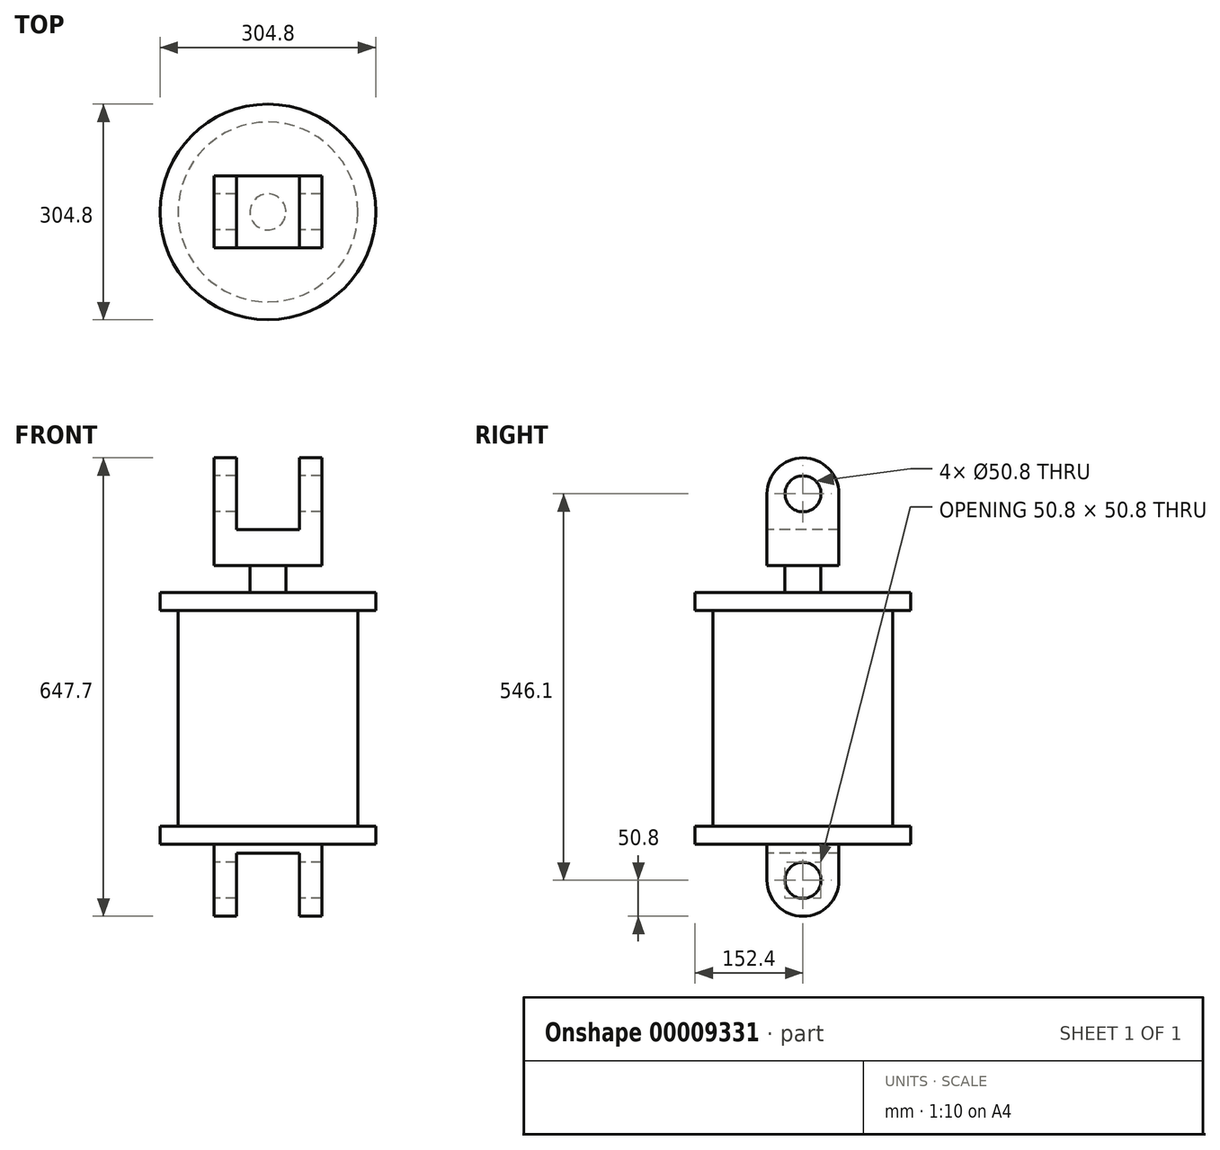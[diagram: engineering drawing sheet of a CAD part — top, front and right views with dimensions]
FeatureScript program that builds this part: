
annotation { "Feature Type Name" : "Feature", "Feature Type Description" : "" }
export const myFeature = defineFeature(function(context is Context, id is Id, definition is map)
    precondition{}
    {
        {
            var Q0;
            Q0=qCreatedBy(makeId("Right.planeOp"),FACE);
            var sketch = newSketch(context, id + "F0", { "sketchPlane" : qUnion([Q0])});
            skCircle(sketch, "E0", {"center": v(0, 0) * mm, "radius": 25.4 * mm});
            skArc(sketch, "E1", {"start": v(-50.8, 0) * mm, "mid": v(0, -50.8) * mm, "end": v(50.8, 0) * mm});
            skLineSegment(sketch, "E2", {"start": v(-50.8, 0) * mm, "end": v(-50.8, 50.8) * mm});
            skLineSegment(sketch, "E3", {"start": v(-50.8, 50.8) * mm, "end": v(50.8, 50.8) * mm});
            skLineSegment(sketch, "E4", {"start": v(50.8, 50.8) * mm, "end": v(50.8, 0) * mm});
            skSolve(sketch);
        }
        {
            var Q0;
            Q0 = qSketchRegion(id + "F0", true);
            extrude(context, id + "F1", {"entities" : qUnion([Q0]), "endBound" : BoundingType.SYMMETRIC, "depth" : 152.4 * mm});
        }
        {
            var Q0;
            Q0=makeQuery(id+"F1.opExtrude","SWEPT_FACE",FACE,{"disambiguationData":[OSD([sQuery(id+"F0.wireOp",EDGE,"E2")])]});
            var sketch = newSketch(context, id + "F2", { "sketchPlane" : qUnion([Q0])});
            skLineSegment(sketch, "E5.bottom", {"start": v(-44.45, 38.1) * mm, "end": v(44.45, 38.1) * mm});
            skLineSegment(sketch, "E5.top", {"start": v(-44.45, -62.27) * mm, "end": v(44.45, -62.27) * mm});
            skLineSegment(sketch, "E5.left", {"start": v(-44.45, 38.1) * mm, "end": v(-44.45, -62.27) * mm});
            skLineSegment(sketch, "E5.right", {"start": v(44.45, 38.1) * mm, "end": v(44.45, -62.27) * mm});
            skLineSegment(sketch, "E6", {"start": v(0, 50.8) * mm, "end": v(0, -95.86) * mm, "construction": true});
            skSolve(sketch);
        }
        {
            var Q0;
            Q0 = qSketchRegion(id + "F2", true);
            extrude(context, id + "F3", {"entities" : qUnion([Q0]), "operationType" : NewBodyOperationType.REMOVE, "endBound" : BoundingType.THROUGH_ALL, "oppositeDirection" : true, "depth" : 25.4 * mm});
        }
        {
            var Q0;
            Q0=makeQuery(id+"F1.opExtrude","SWEPT_FACE",FACE,{"disambiguationData":[OSD([sQuery(id+"F0.wireOp",EDGE,"E3")])]});
            var sketch = newSketch(context, id + "F4", { "sketchPlane" : qUnion([Q0])});
            skCircle(sketch, "E7", {"center": v(0, 0) * mm, "radius": 152.4 * mm});
            skSolve(sketch);
        }
        {
            var Q0;
            Q0 = qSketchRegion(id + "F4", true);
            extrude(context, id + "F5", {"entities" : qUnion([Q0]), "operationType" : NewBodyOperationType.ADD, "depth" : 25.4 * mm});
        }
        {
            var Q0;
            Q0=makeQuery(id+"F5.opExtrude","CAP_FACE",FACE,{"disambiguationData":[OSD([sQuery(id+"F4.wireOp",EDGE,"E7")])],"isStart":false});
            var sketch = newSketch(context, id + "F6", { "sketchPlane" : qUnion([Q0])});
            skCircle(sketch, "E8", {"center": v(0, 0) * mm, "radius": 127 * mm});
            skSolve(sketch);
        }
        {
            var Q0;
            Q0 = qSketchRegion(id + "F6", true);
            extrude(context, id + "F7", {"entities" : qUnion([Q0]), "operationType" : NewBodyOperationType.ADD, "depth" : 304.8 * mm});
        }
        {
            var Q0;
            Q0=makeQuery(id+"F7.opExtrude","CAP_FACE",FACE,{"disambiguationData":[OSD([sQuery(id+"F6.wireOp",EDGE,"E8")])],"isStart":false});
            var sketch = newSketch(context, id + "F8", { "sketchPlane" : qUnion([Q0])});
            skCircle(sketch, "E9.0", {"center": v(0, 0) * mm, "radius": 152.4 * mm});
            skSolve(sketch);
        }
        {
            var Q0;
            Q0 = qSketchRegion(id + "F8", true);
            extrude(context, id + "F9", {"entities" : qUnion([Q0]), "operationType" : NewBodyOperationType.ADD, "depth" : 25.4 * mm});
        }
        {
            var Q0;
            Q0=makeQuery(id+"F9.opExtrude","CAP_FACE",FACE,{"disambiguationData":[OSD([sQuery(id+"F8.wireOp",EDGE,"E9.0")])],"isStart":false});
            var sketch = newSketch(context, id + "F10", { "sketchPlane" : qUnion([Q0])});
            skCircle(sketch, "E10", {"center": v(0, 0) * mm, "radius": 25.4 * mm});
            skSolve(sketch);
        }
        {
            var Q0;
            Q0 = qSketchRegion(id + "F10", true);
            extrude(context, id + "F11", {"entities" : qUnion([Q0]), "operationType" : NewBodyOperationType.ADD, "depth" : 38.1 * mm});
        }
        {
            var Q0;
            Q0=makeQuery(id+"F11.opExtrude","CAP_FACE",FACE,{"disambiguationData":[OSD([sQuery(id+"F10.wireOp",EDGE,"E10")])],"isStart":false});
            var sketch = newSketch(context, id + "F12", { "sketchPlane" : qUnion([Q0])});
            skLineSegment(sketch, "E11.0", {"start": v(76.2, 50.8) * mm, "end": v(-76.2, 50.8) * mm});
            skLineSegment(sketch, "E12.0", {"start": v(76.2, -50.8) * mm, "end": v(76.2, 50.8) * mm});
            skLineSegment(sketch, "E13.0", {"start": v(76.2, -50.8) * mm, "end": v(-76.2, -50.8) * mm});
            skLineSegment(sketch, "E14.0", {"start": v(-76.2, -50.8) * mm, "end": v(-76.2, 50.8) * mm});
            skSolve(sketch);
        }
        {
            var Q0;
            Q0 = qSketchRegion(id + "F12", true);
            extrude(context, id + "F13", {"entities" : qUnion([Q0]), "operationType" : NewBodyOperationType.ADD, "depth" : 152.4 * mm});
        }
        {
            var Q0;
            Q0=makeQuery(id+"F13.opExtrude","SWEPT_FACE",FACE,{"disambiguationData":[OSD([sQuery(id+"F12.wireOp",EDGE,"E13.0")])]});
            var sketch = newSketch(context, id + "F14", { "sketchPlane" : qUnion([Q0])});
            skLineSegment(sketch, "E15.0", {"start": v(-44.45, 769.4) * mm, "end": v(-44.45, 495.3) * mm});
            skLineSegment(sketch, "E16.0", {"start": v(44.45, 777.53) * mm, "end": v(44.45, 495.3) * mm});
            skPoint(sketch, "E17.orphan", {"position": v(-44.45, 38.1) * mm});
            skPoint(sketch, "E18.orphan", {"position": v(44.45, 38.1) * mm});
            skLineSegment(sketch, "E19.0", {"start": v(44.45, 495.3) * mm, "end": v(-44.45, 495.3) * mm});
            skLineSegment(sketch, "E20.trimOffspring", {"start": v(-44.45, 38.1) * mm, "end": v(-44.45, 0) * mm});
            skLineSegment(sketch, "E21.trimOffspring", {"start": v(44.45, 38.1) * mm, "end": v(44.45, 0) * mm});
            skLineSegment(sketch, "E22", {"start": v(-44.45, 769.4) * mm, "end": v(44.45, 777.53) * mm});
            skSolve(sketch);
        }
        {
            var Q0;
            Q0 = qSketchRegion(id + "F14", true);
            extrude(context, id + "F15", {"entities" : qUnion([Q0]), "operationType" : NewBodyOperationType.REMOVE, "endBound" : BoundingType.THROUGH_ALL, "oppositeDirection" : true, "depth" : 25.4 * mm});
        }
        {
            var Q0;
            {var subQ0=sQuery(id+"F12.wireOp",EDGE,"E11.0");var subQ1=sQuery(id+"F12.wireOp",EDGE,"E14.0");Q0=makeQuery(id+"F15.boolean.opBoolean","SPLIT",EDGE,{"disambiguationData":[TD([makeQuery(id+"F13.opExtrude","SWEPT_FACE",FACE,{"disambiguationData":[OSD([subQ1])]})])],"derivedFrom":makeQuery(id+"F13.opExtrude","CAP_EDGE",EDGE,{"disambiguationData":[OSD([subQ0])],"isStart":false})});}
            var Q1;
            {var subQ0=sQuery(id+"F12.wireOp",EDGE,"E11.0");var subQ1=sQuery(id+"F12.wireOp",EDGE,"E12.0");Q1=makeQuery(id+"F15.boolean.opBoolean","SPLIT",EDGE,{"disambiguationData":[TD([makeQuery(id+"F13.opExtrude","SWEPT_FACE",FACE,{"disambiguationData":[OSD([subQ1])]})])],"derivedFrom":makeQuery(id+"F13.opExtrude","CAP_EDGE",EDGE,{"disambiguationData":[OSD([subQ0])],"isStart":false})});}
            var Q2;
            {var subQ0=sQuery(id+"F12.wireOp",EDGE,"E13.0");var subQ1=sQuery(id+"F12.wireOp",EDGE,"E12.0");Q2=makeQuery(id+"F15.boolean.opBoolean","SPLIT",EDGE,{"disambiguationData":[TD([makeQuery(id+"F13.opExtrude","SWEPT_FACE",FACE,{"disambiguationData":[OSD([subQ1])]})])],"derivedFrom":makeQuery(id+"F13.opExtrude","CAP_EDGE",EDGE,{"disambiguationData":[OSD([subQ0])],"isStart":false})});}
            var Q3;
            {var subQ0=sQuery(id+"F12.wireOp",EDGE,"E13.0");var subQ1=sQuery(id+"F12.wireOp",EDGE,"E14.0");Q3=makeQuery(id+"F15.boolean.opBoolean","SPLIT",EDGE,{"disambiguationData":[TD([makeQuery(id+"F13.opExtrude","SWEPT_FACE",FACE,{"disambiguationData":[OSD([subQ1])]})])],"derivedFrom":makeQuery(id+"F13.opExtrude","CAP_EDGE",EDGE,{"disambiguationData":[OSD([subQ0])],"isStart":false})});}
            fillet(context, id + "F16", {"entities" : qUnion([Q0, Q1, Q2, Q3]), "radius" : 50.8 * mm, "tangentPropagation" : true, "allowEdgeOverflow" : false});
        }
        {
            var Q0;
            Q0=makeQuery(id+"F13.opExtrude","SWEPT_FACE",FACE,{"disambiguationData":[OSD([sQuery(id+"F12.wireOp",EDGE,"E14.0")])]});
            var sketch = newSketch(context, id + "F17", { "sketchPlane" : qUnion([Q0])});
            skCircle(sketch, "E23", {"center": v(0, 546.1) * mm, "radius": 25.4 * mm});
            skSolve(sketch);
        }
        {
            var Q0;
            Q0 = qSketchRegion(id + "F17", true);
            extrude(context, id + "F18", {"entities" : qUnion([Q0]), "operationType" : NewBodyOperationType.REMOVE, "endBound" : BoundingType.THROUGH_ALL, "oppositeDirection" : true, "depth" : 25.4 * mm});
        }
    });
